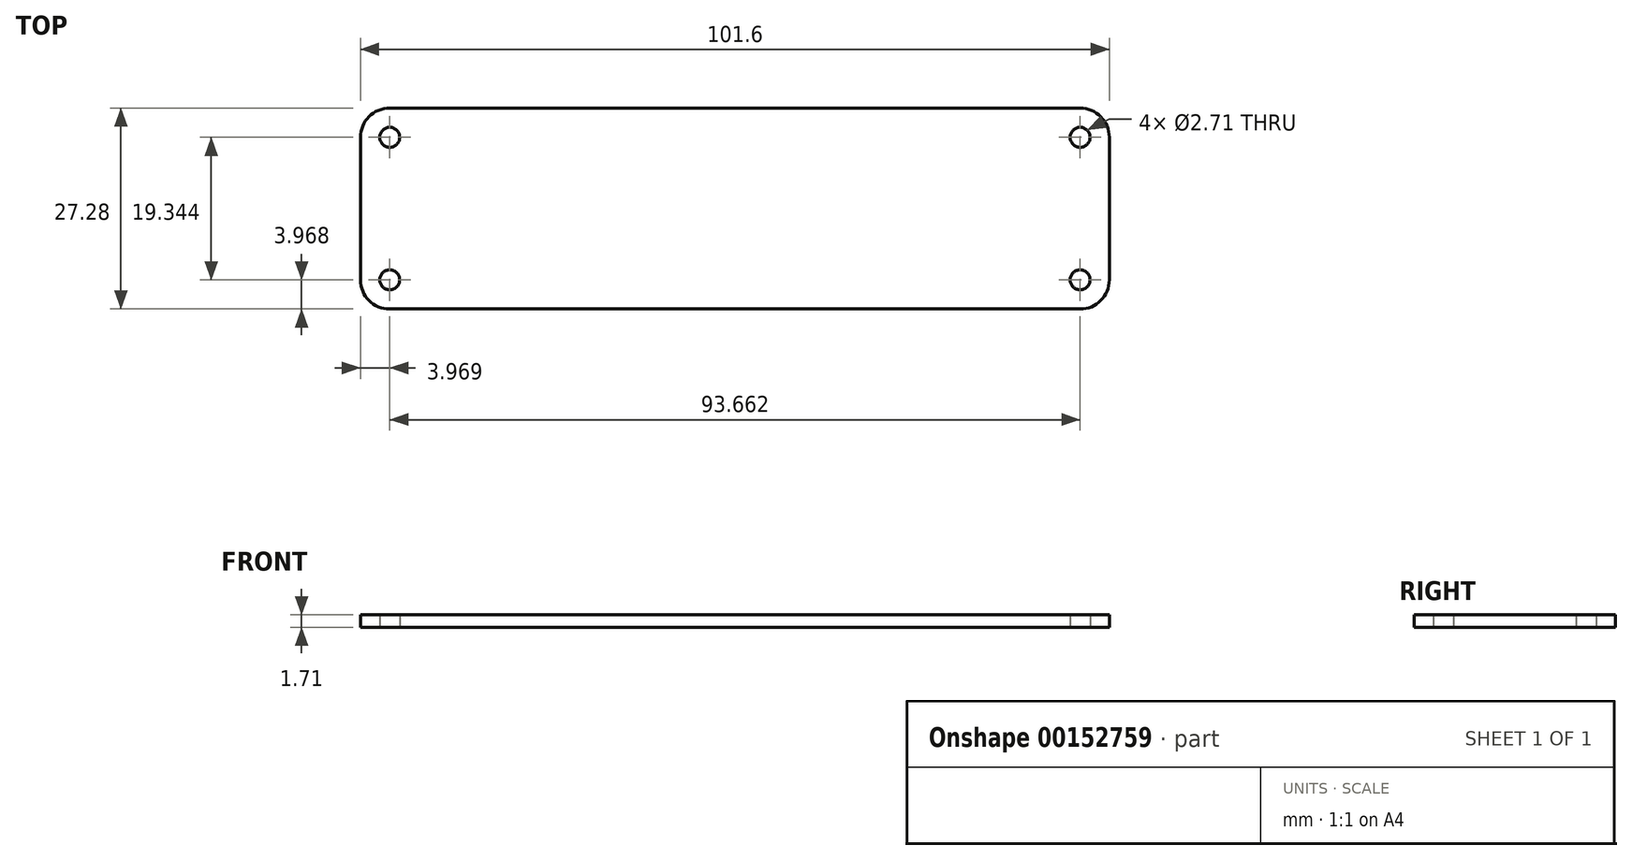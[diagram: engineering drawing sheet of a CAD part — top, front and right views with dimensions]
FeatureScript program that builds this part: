
annotation { "Feature Type Name" : "Feature", "Feature Type Description" : "" }
export const myFeature = defineFeature(function(context is Context, id is Id, definition is map)
    precondition{}
    {
        {
            var Q0;
            Q0=qCreatedBy(makeId("Top.planeOp"),FACE);
            var sketch = newSketch(context, id + "F0", { "sketchPlane" : qUnion([Q0])});
            skLineSegment(sketch, "E0.bottom", {"start": v(-46.83, 9.67) * mm, "end": v(46.83, 9.67) * mm, "construction": true});
            skLineSegment(sketch, "E0.top", {"start": v(-46.83, -9.67) * mm, "end": v(46.83, -9.67) * mm, "construction": true});
            skLineSegment(sketch, "E0.left", {"start": v(-46.83, 9.67) * mm, "end": v(-46.83, -9.67) * mm, "construction": true});
            skLineSegment(sketch, "E0.right", {"start": v(46.83, 9.67) * mm, "end": v(46.83, -9.67) * mm, "construction": true});
            skPoint(sketch, "E0.middle", {"position": v(0, 0) * mm});
            skLineSegment(sketch, "E1", {"start": v(-46.83, 9.67) * mm, "end": v(-46.83, 13.64) * mm, "construction": true});
            skLineSegment(sketch, "E2", {"start": v(-46.83, 9.67) * mm, "end": v(-50.8, 9.67) * mm, "construction": true});
            skLineSegment(sketch, "E3.bottom", {"start": v(-50.8, 13.64) * mm, "end": v(50.8, 13.64) * mm});
            skLineSegment(sketch, "E3.top", {"start": v(-50.8, -13.64) * mm, "end": v(50.8, -13.64) * mm});
            skLineSegment(sketch, "E3.left", {"start": v(-50.8, 13.64) * mm, "end": v(-50.8, -13.64) * mm});
            skLineSegment(sketch, "E3.right", {"start": v(50.8, 13.64) * mm, "end": v(50.8, -13.64) * mm});
            skCircle(sketch, "E4", {"center": v(-46.83, 9.67) * mm, "radius": 1.35 * mm});
            skCircle(sketch, "E5", {"center": v(-46.83, -9.67) * mm, "radius": 1.35 * mm});
            skCircle(sketch, "E6", {"center": v(46.83, -9.67) * mm, "radius": 1.35 * mm});
            skCircle(sketch, "E7", {"center": v(46.83, 9.67) * mm, "radius": 1.35 * mm});
            skSolve(sketch);
        }
        {
            var Q0;
            Q0 = qSketchRegion(id + "F0", true);
            extrude(context, id + "F1", {"entities" : qUnion([Q0]), "depth" : 1.7 * mm});
        }
        {
            var Q0;
            Q0=makeQuery(id+"F1.opExtrude","SWEPT_EDGE",EDGE,{"disambiguationData":[OSD([sQuery(id+"F0.wireOp",EDGE,"E3.bottom"),sQuery(id+"F0.wireOp",EDGE,"E3.left")])]});
            var Q1;
            Q1=makeQuery(id+"F1.opExtrude","SWEPT_EDGE",EDGE,{"disambiguationData":[OSD([sQuery(id+"F0.wireOp",EDGE,"E3.top"),sQuery(id+"F0.wireOp",EDGE,"E3.left")])]});
            var Q2;
            Q2=makeQuery(id+"F1.opExtrude","SWEPT_EDGE",EDGE,{"disambiguationData":[OSD([sQuery(id+"F0.wireOp",EDGE,"E3.top"),sQuery(id+"F0.wireOp",EDGE,"E3.right")])]});
            var Q3;
            Q3=makeQuery(id+"F1.opExtrude","SWEPT_EDGE",EDGE,{"disambiguationData":[OSD([sQuery(id+"F0.wireOp",EDGE,"E3.bottom"),sQuery(id+"F0.wireOp",EDGE,"E3.right")])]});
            fillet(context, id + "F2", {"entities" : qUnion([Q0, Q1, Q2, Q3]), "radius" : 3.97 * mm, "tangentPropagation" : true, "allowEdgeOverflow" : false});
        }
    });
